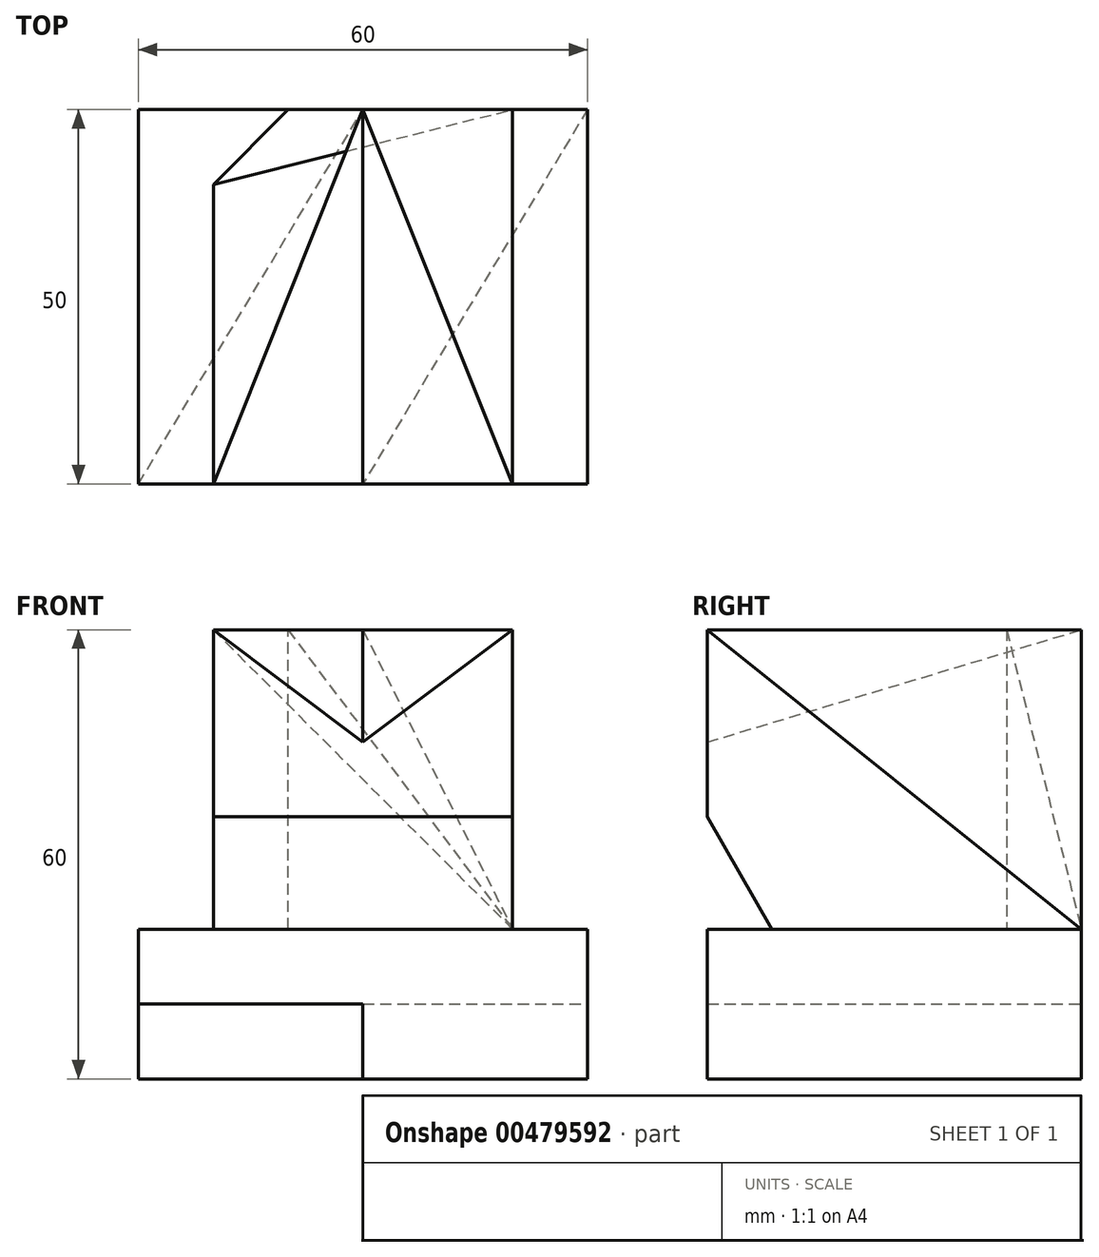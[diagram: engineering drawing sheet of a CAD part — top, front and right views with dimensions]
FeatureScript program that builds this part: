
annotation { "Feature Type Name" : "Feature", "Feature Type Description" : "" }
export const myFeature = defineFeature(function(context is Context, id is Id, definition is map)
    precondition{}
    {
        {
            var Q0;
            Q0=qCreatedBy(makeId("Top.planeOp"),FACE);
            var sketch = newSketch(context, id + "F0", { "sketchPlane" : qUnion([Q0])});
            skLineSegment(sketch, "E0.bottom", {"start": v(0, 0) * mm, "end": v(60, 0) * mm});
            skLineSegment(sketch, "E0.top", {"start": v(0, 50) * mm, "end": v(60, 50) * mm});
            skLineSegment(sketch, "E0.left", {"start": v(0, 0) * mm, "end": v(0, 50) * mm});
            skLineSegment(sketch, "E0.right", {"start": v(60, 0) * mm, "end": v(60, 50) * mm});
            skSolve(sketch);
        }
        {
            var Q0;
            Q0 = qSketchRegion(id + "F0", true);
            extrude(context, id + "F1", {"entities" : qUnion([Q0]), "depth" : 20 * mm});
        }
        {
            var Q0;
            Q0=makeQuery(id+"F1.opExtrude","CAP_FACE",FACE,{"disambiguationData":[OSD([sQuery(id+"F0.wireOp",EDGE,"E0.bottom"),sQuery(id+"F0.wireOp",EDGE,"E0.top"),sQuery(id+"F0.wireOp",EDGE,"E0.left"),sQuery(id+"F0.wireOp",EDGE,"E0.right")])],"isStart":false});
            var sketch = newSketch(context, id + "F2", { "sketchPlane" : qUnion([Q0])});
            skLineSegment(sketch, "E1", {"start": v(10, 0) * mm, "end": v(10, 50) * mm});
            skLineSegment(sketch, "E2", {"start": v(10, 50) * mm, "end": v(50, 50) * mm});
            skLineSegment(sketch, "E3", {"start": v(50, 50) * mm, "end": v(50, 0) * mm});
            skSolve(sketch);
        }
        {
            var Q0;
            Q0 = qSketchRegion(id + "F2", true);
            var Q1;
            {var subQ0=sQuery(id+"F2.wireOp",EDGE,"E1");Q1=makeQuery(id+"F2.imprint","IMPRINT",FACE,{"disambiguationData":[TD([[makeQuery(id+"F2.imprint","IMPRINT",EDGE,{"derivedFrom":subQ0}),-1.0]])]});}
            extrude(context, id + "F3", {"entities" : qUnion([Q0, Q1]), "operationType" : NewBodyOperationType.ADD, "depth" : 40 * mm});
        }
        {
            var Q0;
            Q0=makeQuery(id+"F1.opExtrude","CAP_FACE",FACE,{"disambiguationData":[OSD([sQuery(id+"F0.wireOp",EDGE,"E0.bottom"),sQuery(id+"F0.wireOp",EDGE,"E0.top"),sQuery(id+"F0.wireOp",EDGE,"E0.left"),sQuery(id+"F0.wireOp",EDGE,"E0.right")])],"isStart":true});
            var sketch = newSketch(context, id + "F4", { "sketchPlane" : qUnion([Q0])});
            skLineSegment(sketch, "E4", {"start": v(0, 0) * mm, "end": v(30, -50) * mm});
            skLineSegment(sketch, "E5", {"start": v(30, -50) * mm, "end": v(60, -50) * mm});
            skLineSegment(sketch, "E6", {"start": v(60, -50) * mm, "end": v(30, 0) * mm});
            skLineSegment(sketch, "E7", {"start": v(30, 0) * mm, "end": v(0, 0) * mm});
            skSolve(sketch);
        }
        {
            var Q0;
            Q0 = qSketchRegion(id + "F4", true);
            extrude(context, id + "F5", {"entities" : qUnion([Q0]), "operationType" : NewBodyOperationType.REMOVE, "oppositeDirection" : true, "depth" : 10 * mm});
        }
        {
            var Q0;
            Q0=makeQuery(id+"F3.opExtrude","SWEPT_FACE",FACE,{"disambiguationData":[OSD([sQuery(id+"F2.wireOp",EDGE,"E3")])]});
            var sketch = newSketch(context, id + "F6", { "sketchPlane" : qUnion([Q0])});
            skLineSegment(sketch, "E8", {"start": v(0, 35) * mm, "end": v(8.66, 20) * mm});
            skLineSegment(sketch, "E9", {"start": v(8.66, 20) * mm, "end": v(0, 20) * mm});
            skLineSegment(sketch, "E10", {"start": v(0, 20) * mm, "end": v(0, 35) * mm});
            skSolve(sketch);
        }
        {
            var Q0;
            Q0=makeQuery(id+"F6.imprint","IMPRINT",FACE,{"disambiguationData":[TD([[makeQuery(id+"F6.imprint","IMPRINT",EDGE,{"derivedFrom":sQuery(id+"F6.wireOp",EDGE,"E8")}),-1.0]])]});
            extrude(context, id + "F7", {"entities" : qUnion([Q0]), "operationType" : NewBodyOperationType.REMOVE, "endBound" : BoundingType.UP_TO_NEXT, "oppositeDirection" : true, "depth" : 25 * mm});
        }
        {
            var Q0;
            Q0=makeQuery(id+"F3.opExtrude","CAP_FACE",FACE,{"disambiguationData":[OSD([sQuery(id+"F0.wireOp",EDGE,"E0.bottom"),sQuery(id+"F2.wireOp",EDGE,"E1"),sQuery(id+"F2.wireOp",EDGE,"E2"),sQuery(id+"F2.wireOp",EDGE,"E3")])],"isStart":false});
            var sketch = newSketch(context, id + "F8", { "sketchPlane" : qUnion([Q0])});
            skLineSegment(sketch, "E11", {"start": v(30, 50) * mm, "end": v(10, 0) * mm});
            skLineSegment(sketch, "E12", {"start": v(10, 0) * mm, "end": v(30, 0) * mm});
            skLineSegment(sketch, "E13", {"start": v(30, 0) * mm, "end": v(30, 50) * mm});
            skLineSegment(sketch, "E14", {"start": v(50, 0) * mm, "end": v(30, 50) * mm});
            skSolve(sketch);
        }
        {
            var Q0;
            {var subQ0=sQuery(id+"F2.wireOp",EDGE,"E1");var subQ2=sQuery(id+"F0.wireOp",EDGE,"E0.bottom");Q0=makeQuery(id+"F7.boolean.opBoolean","SPLIT",FACE,{"disambiguationData":[TD([makeQuery(id+"F3.opExtrude","SWEPT_FACE",FACE,{"disambiguationData":[OSD([subQ0])]})])],"derivedFrom":makeQuery(id+"F3.boolean.opBoolean","MERGE",FACE,{"derivedFrom":[makeQuery(id+"F1.opExtrude","SWEPT_FACE",FACE,{"disambiguationData":[OSD([subQ2])]}),makeQuery(id+"F3.opExtrude","SWEPT_FACE",FACE,{"disambiguationData":[OSD([subQ2])]})]})});}
            var sketch = newSketch(context, id + "F9", { "sketchPlane" : qUnion([Q0])});
            skLineSegment(sketch, "E15", {"start": v(10, 60) * mm, "end": v(30, 60) * mm});
            skLineSegment(sketch, "E16", {"start": v(30, 60) * mm, "end": v(30, 45) * mm});
            skLineSegment(sketch, "E17", {"start": v(30, 45) * mm, "end": v(10.47, 60) * mm});
            skLineSegment(sketch, "E18", {"start": v(30, 60) * mm, "end": v(50, 60) * mm});
            skLineSegment(sketch, "E19", {"start": v(50, 60) * mm, "end": v(30, 45) * mm});
            skSolve(sketch);
        }
        {
            var Q0;
            Q0=makeQuery(id+"F3.opExtrude","SWEPT_EDGE",EDGE,{"disambiguationData":[OSD([sQuery(id+"F0.wireOp",EDGE,"E0.top"),sQuery(id+"F2.wireOp",EDGE,"E1"),sQuery(id+"F2.wireOp",EDGE,"E2")])]});
            chamfer(context, id + "F10", {"entities" : qUnion([Q0]), "width" : 10 * mm, "tangentPropagation" : true});
        }
        {
            var Q0;
            Q0=makeQuery(id+"F3.opExtrude","SWEPT_FACE",FACE,{"disambiguationData":[OSD([sQuery(id+"F2.wireOp",EDGE,"E3")])]});
            var sketch = newSketch(context, id + "F11", { "sketchPlane" : qUnion([Q0])});
            skLineSegment(sketch, "E20", {"start": v(50, 60) * mm, "end": v(0, 45) * mm});
            skSolve(sketch);
        }
        {
            var Q0;
            {var subQ0=sQuery(id+"F9.wireOp",EDGE,"E16");Q0=makeQuery(id+"F9.imprint","IMPRINT",FACE,{"disambiguationData":[TD([[makeQuery(id+"F9.imprint","IMPRINT",EDGE,{"derivedFrom":subQ0}),-1.0]])]});}
            var Q1;
            Q1=makeQuery(id+"F9.imprint","IMPRINT",FACE,{"disambiguationData":[TD([[makeQuery(id+"F9.imprint","IMPRINT",EDGE,{"derivedFrom":sQuery(id+"F9.wireOp",EDGE,"E16")}),1.0]])]});
            var Q2;
            Q2=sQuery(id+"F11.wireOp",EDGE,"E20");
            sweep(context, id + "F12", {"operationType" : NewBodyOperationType.REMOVE, "profiles" : qUnion([Q0, Q1]), "path" : qUnion([Q2])});
        }
        {
            var Q0;
            {var subQ0=sQuery(id+"F2.wireOp",EDGE,"E3");var subQ1=sQuery(id+"F0.wireOp",EDGE,"E0.bottom");Q0=makeQuery(id+"F12.boolean.opBoolean","MERGE",VERTEX,{"derivedFrom":[makeQuery(id+"F3.opExtrude","CAP_VERTEX",VERTEX,{"disambiguationData":[OSD([subQ1,subQ0])],"isStart":false}),makeQuery(id+"F12.opSweep","CAP_VERTEX",VERTEX,{"disambiguationData":[OSD([subQ1,subQ0,sQuery(id+"F9.wireOp",EDGE,"E18"),sQuery(id+"F9.wireOp",EDGE,"E19"),sQuery(id+"F11.wireOp",EDGE,"E20")])],"isStart":true})]});}
            var Q1;
            Q1=makeQuery(id+"F3.opExtrude","CAP_VERTEX",VERTEX,{"disambiguationData":[OSD([sQuery(id+"F0.wireOp",EDGE,"E0.top"),sQuery(id+"F2.wireOp",EDGE,"E2"),sQuery(id+"F2.wireOp",EDGE,"E3")])],"isStart":true});
            var Q2;
            Q2=makeQuery(id+"F12.boolean.opBoolean","COPY",VERTEX,{"derivedFrom":makeQuery(id+"F12.opSweep","CAP_VERTEX",VERTEX,{"disambiguationData":[OSD([sQuery(id+"F9.wireOp",EDGE,"E16"),sQuery(id+"F9.wireOp",EDGE,"E17"),sQuery(id+"F9.wireOp",EDGE,"E19"),sQuery(id+"F11.wireOp",EDGE,"E20")])],"isStart":false})});
            cPlane(context, id + "F13", {"entities" : qUnion([Q0, Q1, Q2]), "cplaneType" : CPlaneType.THREE_POINT, "offset" : 25 * mm, "width" : 150 * mm, "height" : 150 * mm});
        }
        {
            var Q0;
            {var subQ0=sQuery(id+"F2.wireOp",EDGE,"E2");var subQ1=sQuery(id+"F2.wireOp",EDGE,"E3");var subQ2=sQuery(id+"F0.wireOp",EDGE,"E0.bottom");var subQ3=makeQuery(id+"F3.opExtrude","CAP_FACE",FACE,{"disambiguationData":[OSD([subQ2,sQuery(id+"F2.wireOp",EDGE,"E1"),subQ0,subQ1])],"isStart":false});Q0=makeQuery(id+"F12.boolean.opBoolean","SPLIT",FACE,{"disambiguationData":[TD([makeQuery(id+"F3.opExtrude","SWEPT_FACE",FACE,{"disambiguationData":[OSD([subQ1])]})])],"derivedFrom":subQ3});}
            var Q1;
            Q1=qCreatedBy(id+"F13.planeOp",FACE);
            extrude(context, id + "F14", {"entities" : qUnion([Q0]), "operationType" : NewBodyOperationType.REMOVE, "endBound" : BoundingType.UP_TO_SURFACE, "oppositeDirection" : true, "depth" : 25 * mm, "endBoundEntityFace" : qUnion([Q1]), "offsetDistance" : 25 * mm});
        }
        {
            var Q1;
            Q1=makeQuery(id+"F8.imprint","IMPRINT",FACE,{"disambiguationData":[TD([[makeQuery(id+"F8.imprint","IMPRINT",EDGE,{"derivedFrom":sQuery(id+"F8.wireOp",EDGE,"E11")}),1.0]])]});
            var Q2;
            Q2=sQuery(id+"F9.wireOp",VERTEX,"E19.end");
            loft(context, id + "F15", {"operationType" : NewBodyOperationType.REMOVE, "sheetProfilesArray" : [{ "sheetProfileEntities" : qUnion([Q1]) }, { "sheetProfileEntities" : qUnion([Q2]) }]});
        }
        {
            var Q1;
            {var subQ0=sQuery(id+"F2.wireOp",EDGE,"E2");var subQ5=sQuery(id+"F0.wireOp",EDGE,"E0.bottom");var subQ6=sQuery(id+"F2.wireOp",EDGE,"E3");var subQ7=sQuery(id+"F2.wireOp",EDGE,"E1");var subQ8=makeQuery(id+"F3.opExtrude","CAP_FACE",FACE,{"disambiguationData":[OSD([subQ5,subQ7,subQ0,subQ6])],"isStart":false});Q1=makeQuery(id+"F15.boolean.opBoolean","SPLIT",FACE,{"disambiguationData":[TD([makeQuery(id+"F3.opExtrude","SWEPT_FACE",FACE,{"disambiguationData":[OSD([subQ6])]})])],"derivedFrom":subQ8});}
            var Q2;
            Q2=makeQuery(id+"F3.opExtrude","CAP_VERTEX",VERTEX,{"disambiguationData":[OSD([sQuery(id+"F0.wireOp",EDGE,"E0.top"),sQuery(id+"F2.wireOp",EDGE,"E2"),sQuery(id+"F2.wireOp",EDGE,"E3")])],"isStart":true});
            loft(context, id + "F16", {"operationType" : NewBodyOperationType.REMOVE, "sheetProfilesArray" : [{ "sheetProfileEntities" : qUnion([Q1]) }, { "sheetProfileEntities" : qUnion([Q2]) }]});
        }
        {
            var Q1;
            {var subQ0=sQuery(id+"F8.wireOp",EDGE,"E13");Q1=makeQuery(id+"F8.imprint","IMPRINT",FACE,{"disambiguationData":[TD([[makeQuery(id+"F8.imprint","IMPRINT",EDGE,{"derivedFrom":subQ0}),-1.0]])]});}
            var Q2;
            Q2=sQuery(id+"F9.wireOp",VERTEX,"E19.end");
            loft(context, id + "F17", {"operationType" : NewBodyOperationType.REMOVE, "sheetProfilesArray" : [{ "sheetProfileEntities" : qUnion([Q1]) }, { "sheetProfileEntities" : qUnion([Q2]) }]});
        }
    });
